# Revit family: PDU básico
name_source: partatom
category: Installations électriques
units: mm (PartAtom-declared; Revit-internal decimal feet)

## family parameters
Basée sur le plan de construction = Non
Conserver l'orientation des annotations = Non
Cote de connecteur circulaire = Utiliser le diamètre
Couper avec des vides une fois chargée = Non
Numéro OmniClass = 23.80.00.00
Partagée = Non
Point de calcul de pièce = Non
Titre OmniClass = Electric Power and Lighting
Toujours verticalement = Oui
Type d'élément = Normal

## types (13) — shared parameters
Clase de aplicación = EC002762
Color = Negro
Conectable con internet box = Non
Consumo pasivo = 0 mA
Dirección de montaje = Vertical
E-catalogo enlace = https://www.legrand.fr
Fabricant = LEGRAND
Formulación BIM = Linkeo DATA CENTER BASIC PDU
Frecuencia eléctrica = 50-50
Función = Unidad DE DISTRIBUTION D'ENERGIE
IP = IP20
Numero RAL = 9017
Programación = Non applicable
Tipo de tensión = AC
zero-valued in all types: Elévation par défaut

## per-type parameters (varying)
- PDU 0U 3P 16A 36xC13+6xC19: 646910=Oui; 646911=Non; 646960=Non; 646961=Non; 646962=Non; 646963=Non; 646964=Non; 646965=Non; 646971=Non; 646972=Non; 646973=Non; 646974=Non; 646975=Non; Anchura (mm)=52 mm  [stored 0.170604 ft]; Corriente de alimentación=16-16; Description=PDU vertical 3 phase 16A with 36 x C13 + 6 x C19 locking outlets IEC60309; EAN=3414971972902; Longitud=1113 mm; Marcaje=Oui; Número de disyuntores=0; Número de fases=3; Número de pieza Legrand=LG-646910; Número de tomas C13=36; Número de tomas C19=6; Prise_alimentation=Alimentation : Prise rotative; Profondeur cuve + capot=65 mm  [stored 0.213255 ft]; Profundidad (mm)=67 mm; Sección de cable MIN_MAX=2.5-2.5; Tipo de conexión eléctrica=CEE 16 A
- PDU 0U 3P 16A 24xC13+12xC19: 646910=Non; 646911=Oui; 646960=Non; 646961=Non; 646962=Non; 646963=Non; 646964=Non; 646965=Non; 646971=Non; 646972=Non; 646973=Non; 646974=Non; 646975=Non; Anchura (mm)=52 mm  [stored 0.170604 ft]; Corriente de alimentación=16-16; Description=PDU vertical 3 phase 16A with 24 x C13 + 12 x C19 locking outlets IEC60309; EAN=3414971972919; Longitud=1131 mm; Marcaje=Oui; Número de disyuntores=0; Número de fases=3; Número de pieza Legrand=LG-646911; Número de tomas C13=24; Número de tomas C19=12; Prise_alimentation=Alimentation : Prise rotative; Profondeur cuve + capot=65 mm  [stored 0.213255 ft]; Profundidad (mm)=67 mm; Sección de cable MIN_MAX=2.5-2.5; Tipo de conexión eléctrica=CEE 16 A
- PDU 0U 1P 16A 18xC13+6xC19: 646910=Non; 646911=Non; 646960=Oui; 646961=Non; 646962=Non; 646963=Non; 646964=Non; 646965=Non; 646971=Non; 646972=Non; 646973=Non; 646974=Non; 646975=Non; Anchura (mm)=44 mm; Corriente de alimentación=16-16; Description=PDU BASIC 0U 1 PHASE 16A , 18+6 C13/C19 LOCKING OUTLETS , IEC 60309; EAN=3414972471374; Longitud=975 mm  [stored 3.19882 ft]; Marcaje=Oui; Número de disyuntores=0; Número de fases=1; Número de pieza Legrand=LG-646960; Número de tomas C13=18; Número de tomas C19=6; Prise_alimentation=Alimentation : Prise rotative; Profondeur cuve + capot=58 mm; Profundidad (mm)=60 mm; Sección de cable MIN_MAX=2.5-2.5; Tipo de conexión eléctrica=CEE 16 A
- PDU 0U 1P 16A 20xC13+4xC19: 646910=Non; 646911=Non; 646960=Non; 646961=Oui; 646962=Non; 646963=Non; 646964=Non; 646965=Non; 646971=Non; 646972=Non; 646973=Non; 646974=Non; 646975=Non; Anchura (mm)=44 mm; Corriente de alimentación=16-16; Description=PDU BASIC 0U 1 PHASE 16A , 20+4 C13/C19 LOCKING OUTLETS , IEC-320 C20; EAN=3414972471381; Longitud=902 mm; Marcaje=Non; Número de disyuntores=0; Número de fases=1; Número de pieza Legrand=LG-646961; Número de tomas C13=20; Número de tomas C19=4; Prise_alimentation=Alimentation : Prise rectangulaire; Profondeur cuve + capot=58 mm; Profundidad (mm)=60 mm; Sección de cable MIN_MAX=1.5-2.5; Tipo de conexión eléctrica=C20
- PDU 0U 1P 32A 20xC13+4xC19: 646910=Non; 646911=Non; 646960=Non; 646961=Non; 646962=Oui; 646963=Non; 646964=Non; 646965=Non; 646971=Non; 646972=Non; 646973=Non; 646974=Non; 646975=Non; Anchura (mm)=44 mm; Corriente de alimentación=32-32; Description=PDU BASIC 0U 1 PHASE 32A , 20+4 C13/C19 LOCKING OUTLETS , IEC 60309; EAN=3414972471398; Longitud=1092 mm; Marcaje=Oui; Número de disyuntores=2; Número de fases=1; Número de pieza Legrand=LG-646962; Número de tomas C13=20; Número de tomas C19=4; Prise_alimentation=Alimentation : Prise rotative; Profondeur cuve + capot=58 mm; Profundidad (mm)=75 mm; Sección de cable MIN_MAX=6-6; Tipo de conexión eléctrica=CEE 32 A
- PDU 0U 1P 32A 12xC13+12xC19: 646910=Non; 646911=Non; 646960=Non; 646961=Non; 646962=Non; 646963=Oui; 646964=Non; 646965=Non; 646971=Non; 646972=Non; 646973=Non; 646974=Non; 646975=Non; Anchura (mm)=44 mm; Corriente de alimentación=32-32; Description=PDU BASIC 0U 1 PHASE 32A , 12+12 C13/C19 LOCKING OUTLETS , IEC 60309; EAN=3414972471404; Longitud=1164 mm; Marcaje=Oui; Número de disyuntores=2; Número de fases=1; Número de pieza Legrand=LG-646963; Número de tomas C13=12; Número de tomas C19=12; Prise_alimentation=Alimentation : Prise rotative; Profondeur cuve + capot=58 mm; Profundidad (mm)=75 mm; Sección de cable MIN_MAX=6-6; Tipo de conexión eléctrica=CEE 16 A
- PDU 0U 3P 16A 21xC13+3xC19: 646910=Non; 646911=Non; 646960=Non; 646961=Non; 646962=Non; 646963=Non; 646964=Oui; 646965=Non; 646971=Non; 646972=Non; 646973=Non; 646974=Non; 646975=Non; Anchura (mm)=44 mm; Corriente de alimentación=16-16; Description=PDU BASIC 0U 3 PHASE 16A , 21+3 C13/C19 LOCKING OUTLETS , IEC 60309; EAN=3414972471411; Longitud=978 mm; Marcaje=Oui; Número de disyuntores=0; Número de fases=3; Número de pieza Legrand=LG-646964; Número de tomas C13=21; Número de tomas C19=3; Prise_alimentation=Alimentation : Prise rotative; Profondeur cuve + capot=58 mm; Profundidad (mm)=60 mm; Sección de cable MIN_MAX=2.5-2.5; Tipo de conexión eléctrica=CEE 16 A
- PDU 0U 3P 16A 24xC13+6xC19: 646910=Non; 646911=Non; 646960=Non; 646961=Non; 646962=Non; 646963=Non; 646964=Non; 646965=Oui; 646971=Non; 646972=Non; 646973=Non; 646974=Non; 646975=Non; Anchura (mm)=44 mm; Corriente de alimentación=16-16; Description=PDU BASIC 0U 3 PHASE 16A , 24+6 C13/C19 LOCKING OUTLETS , IEC 60309; EAN=3414972471428; Longitud=1203 mm; Marcaje=Oui; Número de disyuntores=0; Número de fases=3; Número de pieza Legrand=LG-646965; Número de tomas C13=24; Número de tomas C19=6; Prise_alimentation=Alimentation : Prise rotative; Profondeur cuve + capot=58 mm; Profundidad (mm)=60 mm; Sección de cable MIN_MAX=2.5-2.5; Tipo de conexión eléctrica=CEE 16 A
- PDU HD 0U 1P 32A 24xC13+12xC19: 646910=Non; 646911=Non; 646960=Non; 646961=Non; 646962=Non; 646963=Non; 646964=Non; 646965=Non; 646971=Oui; 646972=Non; 646973=Non; 646974=Non; 646975=Non; Anchura (mm)=52 mm  [stored 0.170604 ft]; Corriente de alimentación=32-32; Description=PDU HD BASIC 0U 1 PHASE 32A , 24+12 C13/C19  LOCKING OUTLETS , IEC 60309; EAN=3414972471459; Longitud=1236 mm; Marcaje=Oui; Número de disyuntores=2; Número de fases=1; Número de pieza Legrand=LG-646971; Número de tomas C13=24; Número de tomas C19=12; Prise_alimentation=Alimentation : Prise rotative; Profondeur cuve + capot=65 mm  [stored 0.213255 ft]; Profundidad (mm)=82 mm; Sección de cable MIN_MAX=6-6; Tipo de conexión eléctrica=CEE 32 A
- PDU HD 0U 1P 32A 36xC13+6xC19: 646910=Non; 646911=Non; 646960=Non; 646961=Non; 646962=Non; 646963=Non; 646964=Non; 646965=Non; 646971=Non; 646972=Oui; 646973=Non; 646974=Non; 646975=Non; Anchura (mm)=52 mm  [stored 0.170604 ft]; Corriente de alimentación=32-32; Description=PDU HD BASIC 0U 1 PHASE 32A , 36+6 C13/C19  LOCKING OUTLETS , IEC 60309; EAN=3414972471466; Longitud=1218 mm; Marcaje=Oui; Número de disyuntores=2; Número de fases=1; Número de pieza Legrand=LG-646972; Número de tomas C13=36; Número de tomas C19=6; Prise_alimentation=Alimentation : Prise rotative; Profondeur cuve + capot=65 mm  [stored 0.213255 ft]; Profundidad (mm)=82 mm; Sección de cable MIN_MAX=6-6; Tipo de conexión eléctrica=CEE 32 A
- PDU HD 0U 3P 32A 24xC13+12xC19: 646910=Non; 646911=Non; 646960=Non; 646961=Non; 646962=Non; 646963=Non; 646964=Non; 646965=Non; 646971=Non; 646972=Non; 646973=Oui; 646974=Non; 646975=Non; Anchura (mm)=52 mm  [stored 0.170604 ft]; Corriente de alimentación=32-32; Description=PDU HD BASIC 0U 3 PHASE 32A , 24+12 C13/C19 LOCKING OUTLETS, IEC 60309; EAN=3414972471473; Longitud=1506 mm; Marcaje=Oui; Número de disyuntores=6; Número de fases=3; Número de pieza Legrand=LG-646973; Número de tomas C13=24; Número de tomas C19=12; Prise_alimentation=Alimentation : Prise rotative; Profondeur cuve + capot=65 mm  [stored 0.213255 ft]; Profundidad (mm)=82 mm; Sección de cable MIN_MAX=6-6; Tipo de conexión eléctrica=CEE 32 A
- PDU HD 0U 3P 32A 36xC13+12xC19: 646910=Non; 646911=Non; 646960=Non; 646961=Non; 646962=Non; 646963=Non; 646964=Non; 646965=Non; 646971=Non; 646972=Non; 646973=Non; 646974=Oui; 646975=Non; Anchura (mm)=52 mm  [stored 0.170604 ft]; Corriente de alimentación=32-32; Description=PDU HD BASIC 0U 3 PHASE 32A , 36+12 C13/C19 LOCKING OUTLETS, IEC 60309; EAN=3414972471480; Longitud=1740 mm; Marcaje=Oui; Número de disyuntores=6; Número de fases=3; Número de pieza Legrand=LG-646974; Número de tomas C13=36; Número de tomas C19=12; Prise_alimentation=Alimentation : Prise rotative; Profondeur cuve + capot=65 mm  [stored 0.213255 ft]; Profundidad (mm)=82 mm; Sección de cable MIN_MAX=6-6; Tipo de conexión eléctrica=CEE 32 A
- PDU HD 0U 3P 32A 36xC13+6xC19: 646910=Non; 646911=Non; 646960=Non; 646961=Non; 646962=Non; 646963=Non; 646964=Non; 646965=Non; 646971=Non; 646972=Non; 646973=Non; 646974=Non; 646975=Oui; Anchura (mm)=52 mm  [stored 0.170604 ft]; Corriente de alimentación=32-32; Description=PDU HD BASIC 0U 3 PHASE 32A , 36+6 C13/C19 LOCKING OUTLETS, IEC 60309; EAN=3414972471497; Longitud=1488 mm  [stored 4.88189 ft]; Marcaje=Oui; Número de disyuntores=6; Número de fases=3; Número de pieza Legrand=LG-646975; Número de tomas C13=36; Número de tomas C19=6; Prise_alimentation=Alimentation : Prise rotative; Profondeur cuve + capot=65 mm  [stored 0.213255 ft]; Profundidad (mm)=82 mm; Sección de cable MIN_MAX=6-6; Tipo de conexión eléctrica=CEE 32 A

note: [stored X ft] marks values corroborated as IEEE doubles in the binary element streams (Revit-internal decimal feet)
